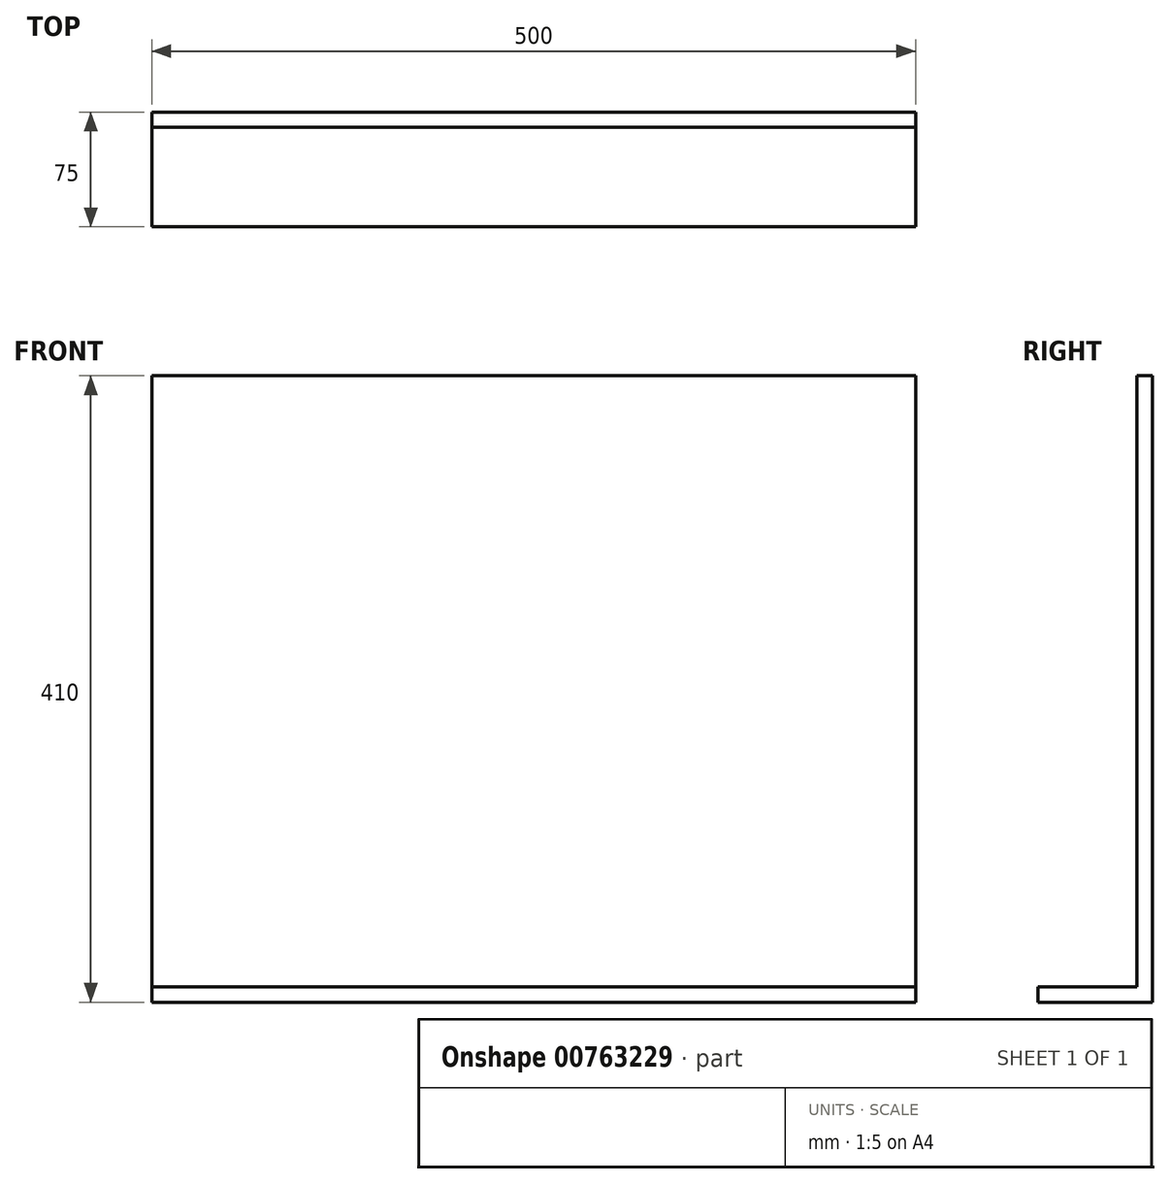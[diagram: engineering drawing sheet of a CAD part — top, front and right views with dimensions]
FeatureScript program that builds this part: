
annotation { "Feature Type Name" : "Feature", "Feature Type Description" : "" }
export const myFeature = defineFeature(function(context is Context, id is Id, definition is map)
    precondition{}
    {
        {
            var Q0;
            Q0=qCreatedBy(makeId("Right.planeOp"),FACE);
            var sketch = newSketch(context, id + "F0", { "sketchPlane" : qUnion([Q0])});
            skLineSegment(sketch, "E0", {"start": v(0, 0) * mm, "end": v(-65, 0) * mm});
            skLineSegment(sketch, "E1", {"start": v(-65, 0) * mm, "end": v(-65, -10) * mm});
            skLineSegment(sketch, "E2", {"start": v(-65, -10) * mm, "end": v(10, -10) * mm});
            skLineSegment(sketch, "E3", {"start": v(10, -10) * mm, "end": v(10, 400) * mm});
            skLineSegment(sketch, "E4", {"start": v(10, 400) * mm, "end": v(0, 400) * mm});
            skLineSegment(sketch, "E5", {"start": v(0, 400) * mm, "end": v(0, 0) * mm});
            skSolve(sketch);
        }
        {
            var Q0;
            Q0=qSketchRegion(id+"F0",true);
            extrude(context, id + "F1", {"entities" : qUnion([Q0]), "endBound" : BoundingType.SYMMETRIC, "depth" : 500 * mm, "offsetDistance" : 25 * mm});
        }
        {
            var Q0;
            Q0=makeQuery(id+"F1.opExtrude","SWEPT_FACE",FACE,{"disambiguationData":[OSD([sQuery(id+"F0.wireOp",EDGE,"E5")])]});
            var sketch = newSketch(context, id + "F2", { "sketchPlane" : qUnion([Q0])});
            skLineSegment(sketch, "E6", {"start": v(0, 0) * mm, "end": v(0, 400) * mm, "construction": true});
            skPoint(sketch, "E7", {"position": v(0, 15) * mm});
            skPoint(sketch, "E8", {"position": v(0, 315) * mm});
            skSolve(sketch);
        }
    });
